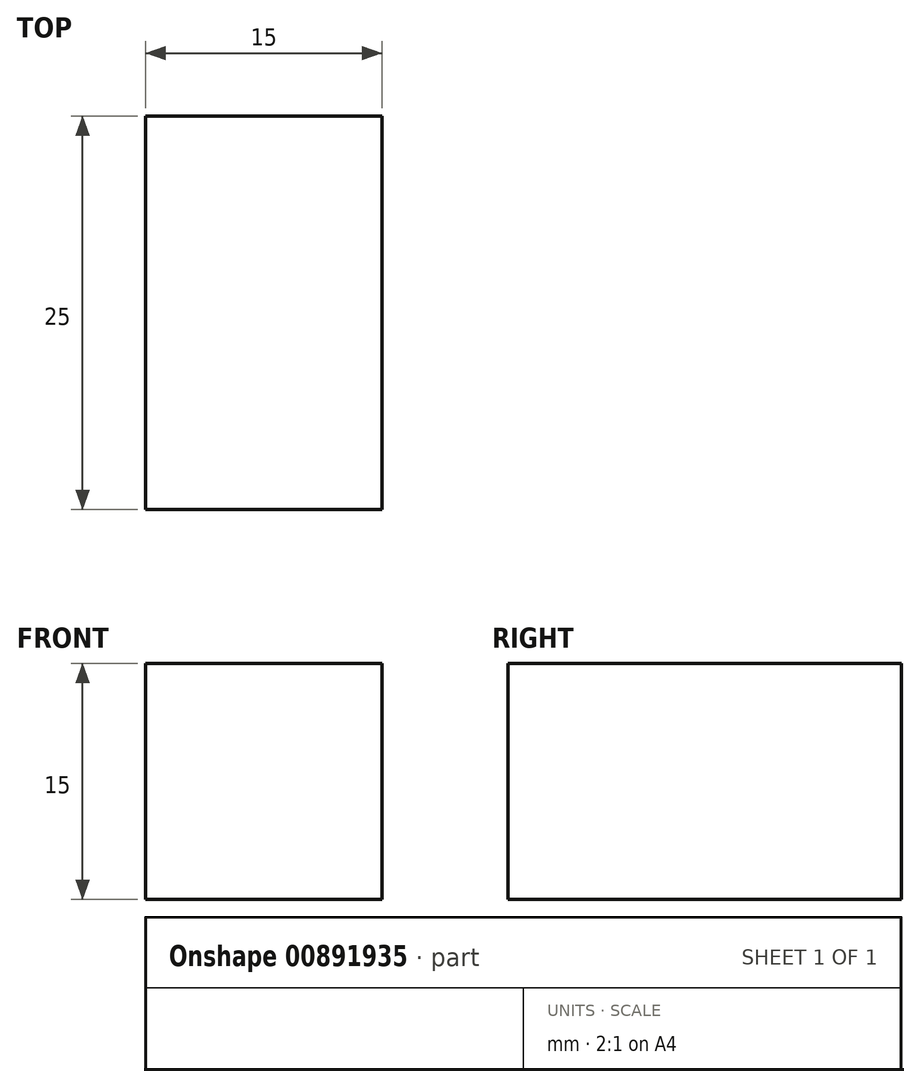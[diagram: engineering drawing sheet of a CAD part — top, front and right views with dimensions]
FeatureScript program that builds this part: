
annotation { "Feature Type Name" : "Feature", "Feature Type Description" : "" }
export const myFeature = defineFeature(function(context is Context, id is Id, definition is map)
    precondition{}
    {
        {
            var Q0;
            Q0=qCreatedBy(makeId("Front.planeOp"),FACE);
            var sketch = newSketch(context, id + "F0", { "sketchPlane" : qUnion([Q0])});
            skLineSegment(sketch, "E0.bottom", {"start": v(7.5, 7.5) * mm, "end": v(-7.5, 7.5) * mm});
            skLineSegment(sketch, "E0.top", {"start": v(7.5, -7.5) * mm, "end": v(-7.5, -7.5) * mm});
            skLineSegment(sketch, "E0.left", {"start": v(7.5, 7.5) * mm, "end": v(7.5, -7.5) * mm});
            skLineSegment(sketch, "E0.right", {"start": v(-7.5, 7.5) * mm, "end": v(-7.5, -7.5) * mm});
            skPoint(sketch, "E0.middle", {"position": v(0, 0) * mm});
            skSolve(sketch);
        }
        {
            var Q0;
            Q0 = qSketchRegion(id + "F0", true);
            extrude(context, id + "F1", {"entities" : qUnion([Q0]), "depth" : 25 * mm, "offsetDistance" : 25 * mm});
        }
    });
